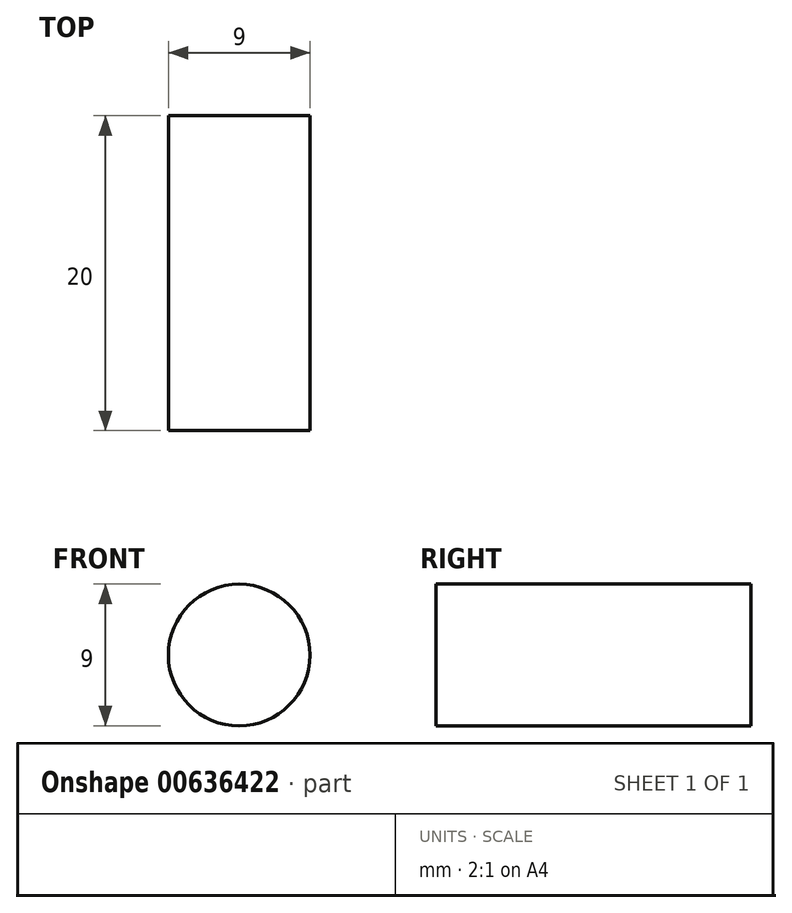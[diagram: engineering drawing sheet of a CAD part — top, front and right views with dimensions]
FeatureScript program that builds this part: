
annotation { "Feature Type Name" : "Feature", "Feature Type Description" : "" }
export const myFeature = defineFeature(function(context is Context, id is Id, definition is map)
    precondition{}
    {
        {
            var Q0;
            Q0=qCreatedBy(makeId("Front.planeOp"),FACE);
            var sketch = newSketch(context, id + "F0", { "sketchPlane" : qUnion([Q0])});
            skCircle(sketch, "E0", {"center": v(-21.76, 22.06) * mm, "radius": 4.5 * mm});
            skSolve(sketch);
        }
        {
            var Q0;
            Q0=makeQuery(id+"F0.imprint","IMPRINT",FACE,{"disambiguationData":[TD([[makeQuery(id+"F0.imprint","IMPRINT",EDGE,{"derivedFrom":sQuery(id+"F0.wireOp",EDGE,"E0")}),1.0]])]});
            extrude(context, id + "F1", {"entities" : qUnion([Q0]), "depth" : 20 * mm, "offsetDistance" : 25 * mm});
        }
    });
